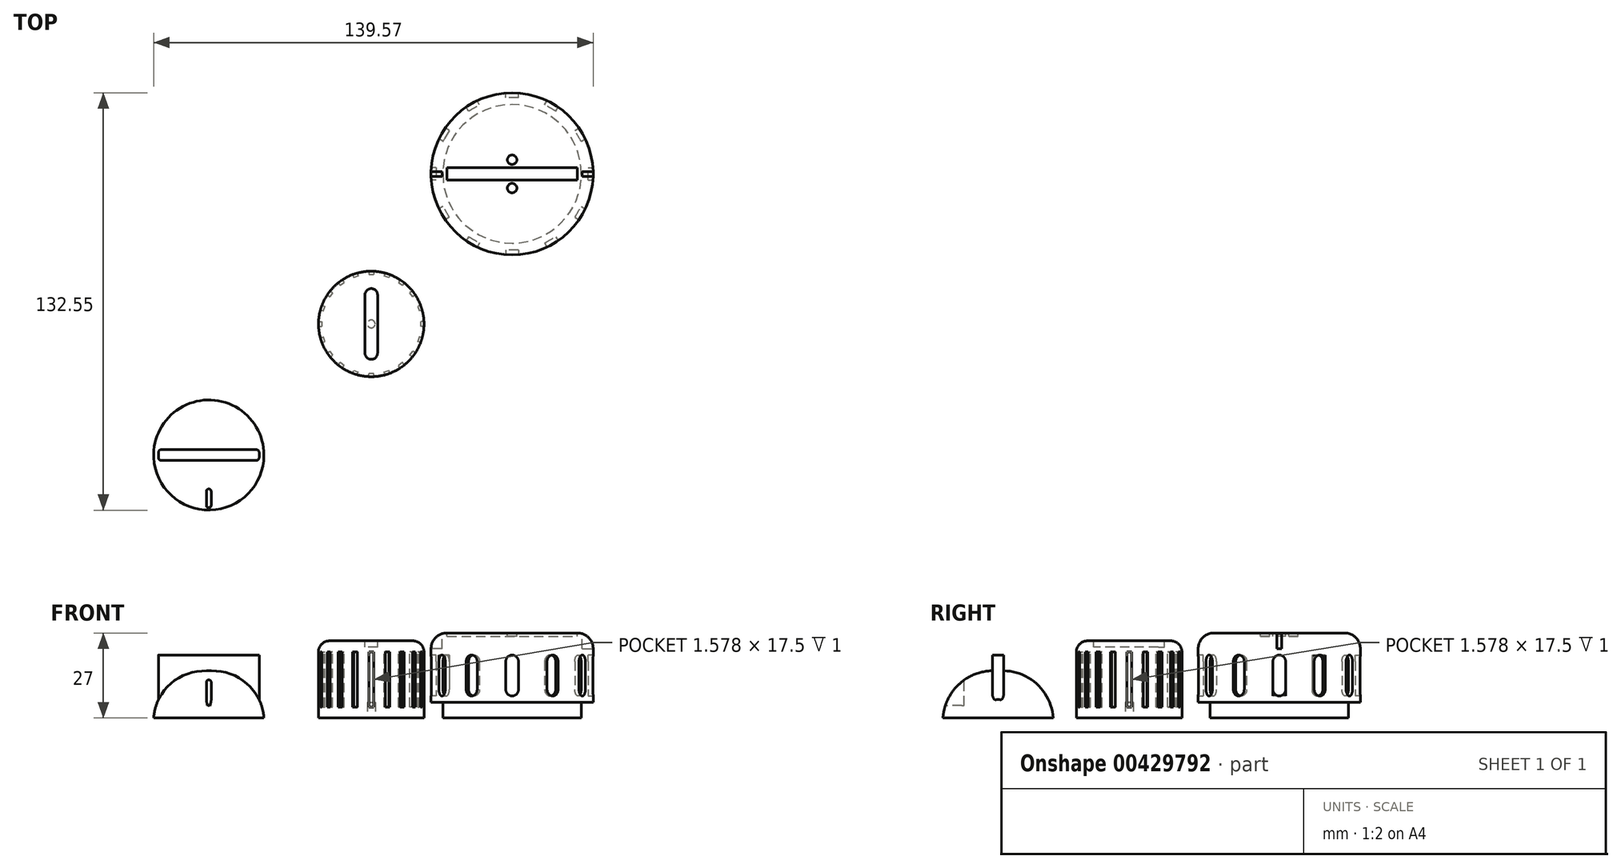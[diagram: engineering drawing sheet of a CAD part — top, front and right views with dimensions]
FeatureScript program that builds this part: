
annotation { "Feature Type Name" : "Feature", "Feature Type Description" : "" }
export const myFeature = defineFeature(function(context is Context, id is Id, definition is map)
    precondition{}
    {
        {
            var Q0;
            Q0=qCreatedBy(makeId("Top.planeOp"),FACE);
            var sketch = newSketch(context, id + "F0", { "sketchPlane" : qUnion([Q0])});
            skCircle(sketch, "E0", {"center": v(0, 0) * mm, "radius": 16.75 * mm});
            skSolve(sketch);
        }
        {
            var Q0;
            Q0=makeQuery(id+"F0.imprint","IMPRINT",FACE,{"disambiguationData":[TD([[makeQuery(id+"F0.imprint","IMPRINT",EDGE,{"derivedFrom":sQuery(id+"F0.wireOp",EDGE,"E0")}),1.0]])]});
            extrude(context, id + "F1", {"entities" : qUnion([Q0]), "depth" : 21 * mm});
        }
        {
            var Q0;
            Q0=makeQuery(id+"F1.opExtrude","CAP_FACE",FACE,{"disambiguationData":[OSD([sQuery(id+"F0.wireOp",EDGE,"E0")])],"isStart":false});
            var sketch = newSketch(context, id + "F2", { "sketchPlane" : qUnion([Q0])});
            skSolve(sketch);
        }
        {
            var Q0;
            Q0=makeQuery(id+"F1.opExtrude","CAP_FACE",FACE,{"disambiguationData":[OSD([sQuery(id+"F0.wireOp",EDGE,"E0")])],"isStart":false});
            var sketch = newSketch(context, id + "F3", { "sketchPlane" : qUnion([Q0])});
            skLineSegment(sketch, "E1", {"start": v(0, 0) * mm, "end": v(0, 16.75) * mm, "construction": true});
            skLineSegment(sketch, "E2", {"start": v(0, 0) * mm, "end": v(-0.79, 16.73) * mm, "construction": true});
            skLineSegment(sketch, "E3", {"start": v(0, 0) * mm, "end": v(0.79, 16.73) * mm, "construction": true});
            skLineSegment(sketch, "E4", {"start": v(0, 0) * mm, "end": v(4.42, 16.16) * mm, "construction": true});
            skLineSegment(sketch, "E5", {"start": v(0.79, 16.73) * mm, "end": v(0.79, 15.73) * mm});
            skLineSegment(sketch, "E6", {"start": v(-0.79, 16.73) * mm, "end": v(-0.79, 15.73) * mm});
            skLineSegment(sketch, "E7", {"start": v(-0.79, 15.73) * mm, "end": v(0.79, 15.73) * mm});
            skArc(sketch, "E8", {"start": v(0.79, 16.73) * mm, "mid": v(0, 16.75) * mm, "end": v(-0.79, 16.73) * mm});
            skLineSegment(sketch, "E9", {"start": v(0, 0) * mm, "end": v(2.62, 16.54) * mm, "construction": true});
            skArc(sketch, "E10.MirrorCS", {"start": v(4.42, 16.16) * mm, "mid": v(5.18, 15.93) * mm, "end": v(5.92, 15.67) * mm});
            skLineSegment(sketch, "E11.MirrorCS", {"start": v(4.42, 16.16) * mm, "end": v(4.11, 15.2) * mm});
            skLineSegment(sketch, "E12.MirrorCS", {"start": v(5.92, 15.67) * mm, "end": v(5.61, 14.72) * mm});
            skLineSegment(sketch, "E13.MirrorCS", {"start": v(5.61, 14.72) * mm, "end": v(4.11, 15.2) * mm});
            skLineSegment(sketch, "E14", {"start": v(0, 0) * mm, "end": v(7.6, 14.92) * mm, "construction": true});
            skLineSegment(sketch, "E15.MirrorCS", {"start": v(10.47, 13.07) * mm, "end": v(9.89, 12.26) * mm});
            skLineSegment(sketch, "E16.MirrorCS", {"start": v(8.6, 13.2) * mm, "end": v(9.89, 12.26) * mm});
            skLineSegment(sketch, "E17.MirrorCS", {"start": v(9.2, 14) * mm, "end": v(8.6, 13.2) * mm});
            skArc(sketch, "E18.MirrorCS", {"start": v(10.47, 13.07) * mm, "mid": v(9.85, 13.55) * mm, "end": v(9.2, 14) * mm});
            skArc(sketch, "E19.MirrorCS", {"start": v(13.07, 10.47) * mm, "mid": v(13.55, 9.85) * mm, "end": v(14, 9.2) * mm});
            skLineSegment(sketch, "E20.MirrorCS", {"start": v(13.07, 10.47) * mm, "end": v(12.26, 9.89) * mm});
            skLineSegment(sketch, "E21.MirrorCS", {"start": v(14, 9.2) * mm, "end": v(13.2, 8.6) * mm});
            skLineSegment(sketch, "E22.MirrorCS", {"start": v(13.2, 8.6) * mm, "end": v(12.26, 9.89) * mm});
            skLineSegment(sketch, "E23", {"start": v(13.07, 10.47) * mm, "end": v(0, 0) * mm, "construction": true});
            skLineSegment(sketch, "E24", {"start": v(14.92, 7.6) * mm, "end": v(0, 0) * mm, "construction": true});
            skArc(sketch, "E25.MirrorCS", {"start": v(16.16, 4.42) * mm, "mid": v(15.93, 5.18) * mm, "end": v(15.67, 5.92) * mm});
            skLineSegment(sketch, "E26.MirrorCS", {"start": v(15.67, 5.92) * mm, "end": v(14.72, 5.61) * mm});
            skLineSegment(sketch, "E27.MirrorCS", {"start": v(14.72, 5.61) * mm, "end": v(15.2, 4.11) * mm});
            skLineSegment(sketch, "E28.MirrorCS", {"start": v(16.16, 4.42) * mm, "end": v(15.2, 4.11) * mm});
            skLineSegment(sketch, "E29.MirrorCS", {"start": v(16.73, -0.79) * mm, "end": v(15.73, -0.79) * mm});
            skLineSegment(sketch, "E30.MirrorCS", {"start": v(15.73, -0.79) * mm, "end": v(15.73, 0.79) * mm});
            skLineSegment(sketch, "E31.MirrorCS", {"start": v(16.73, 0.79) * mm, "end": v(15.73, 0.79) * mm});
            skArc(sketch, "E32.MirrorCS", {"start": v(16.73, 0.79) * mm, "mid": v(16.75, 0) * mm, "end": v(16.73, -0.79) * mm});
            skArc(sketch, "E33.MirrorCS", {"start": v(15.67, -5.92) * mm, "mid": v(15.93, -5.18) * mm, "end": v(16.16, -4.42) * mm});
            skLineSegment(sketch, "E34.MirrorCS", {"start": v(16.16, -4.42) * mm, "end": v(15.2, -4.11) * mm});
            skLineSegment(sketch, "E35.MirrorCS", {"start": v(15.2, -4.11) * mm, "end": v(14.72, -5.61) * mm});
            skLineSegment(sketch, "E36.MirrorCS", {"start": v(15.67, -5.92) * mm, "end": v(14.72, -5.61) * mm});
            skArc(sketch, "E37.MirrorCS", {"start": v(14, -9.2) * mm, "mid": v(13.55, -9.85) * mm, "end": v(13.07, -10.47) * mm});
            skLineSegment(sketch, "E38.MirrorCS", {"start": v(13.07, -10.47) * mm, "end": v(12.26, -9.89) * mm});
            skLineSegment(sketch, "E39.MirrorCS", {"start": v(14, -9.2) * mm, "end": v(13.2, -8.6) * mm});
            skLineSegment(sketch, "E40.MirrorCS", {"start": v(12.26, -9.89) * mm, "end": v(13.2, -8.6) * mm});
            skLineSegment(sketch, "E41", {"start": v(0, 0) * mm, "end": v(14, -9.2) * mm, "construction": true});
            skLineSegment(sketch, "E42", {"start": v(0, 0) * mm, "end": v(11.84, -11.84) * mm, "construction": true});
            skLineSegment(sketch, "E43.MirrorCS", {"start": v(-10.47, -13.07) * mm, "end": v(-9.89, -12.26) * mm});
            skLineSegment(sketch, "E44.MirrorCS", {"start": v(-0.79, -16.73) * mm, "end": v(-0.79, -15.73) * mm});
            skArc(sketch, "E45.MirrorCS", {"start": v(-10.47, -13.07) * mm, "mid": v(-9.85, -13.55) * mm, "end": v(-9.2, -14) * mm});
            skLineSegment(sketch, "E46.MirrorCS", {"start": v(-13.07, -10.47) * mm, "end": v(-12.26, -9.89) * mm});
            skLineSegment(sketch, "E47.MirrorCS", {"start": v(-13.2, -8.6) * mm, "end": v(-12.26, -9.89) * mm});
            skLineSegment(sketch, "E48.MirrorCS", {"start": v(-16.16, -4.42) * mm, "end": v(-15.2, -4.11) * mm});
            skLineSegment(sketch, "E49.MirrorCS", {"start": v(-5.61, -14.72) * mm, "end": v(-4.11, -15.2) * mm});
            skLineSegment(sketch, "E50.MirrorCS", {"start": v(9.89, -12.26) * mm, "end": v(8.6, -13.2) * mm});
            skLineSegment(sketch, "E51.MirrorCS", {"start": v(-5.92, -15.67) * mm, "end": v(-5.61, -14.72) * mm});
            skLineSegment(sketch, "E52.MirrorCS", {"start": v(-16.73, 0.79) * mm, "end": v(-15.73, 0.79) * mm});
            skLineSegment(sketch, "E53.MirrorCS", {"start": v(0.79, -15.73) * mm, "end": v(-0.79, -15.73) * mm});
            skLineSegment(sketch, "E54.MirrorCS", {"start": v(4.11, -15.2) * mm, "end": v(5.61, -14.72) * mm});
            skArc(sketch, "E55.MirrorCS", {"start": v(-4.42, -16.16) * mm, "mid": v(-5.18, -15.93) * mm, "end": v(-5.92, -15.67) * mm});
            skLineSegment(sketch, "E56.MirrorCS", {"start": v(-9.2, -14) * mm, "end": v(-8.6, -13.2) * mm});
            skLineSegment(sketch, "E57.MirrorCS", {"start": v(-8.6, -13.2) * mm, "end": v(-9.89, -12.26) * mm});
            skLineSegment(sketch, "E58.MirrorCS", {"start": v(5.92, -15.67) * mm, "end": v(5.61, -14.72) * mm});
            skLineSegment(sketch, "E59.MirrorCS", {"start": v(-15.67, -5.92) * mm, "end": v(-14.72, -5.61) * mm});
            skArc(sketch, "E60.MirrorCS", {"start": v(5.92, -15.67) * mm, "mid": v(5.18, -15.93) * mm, "end": v(4.42, -16.16) * mm});
            skLineSegment(sketch, "E61.MirrorCS", {"start": v(-14, -9.2) * mm, "end": v(-13.2, -8.6) * mm});
            skLineSegment(sketch, "E62.MirrorCS", {"start": v(-4.42, -16.16) * mm, "end": v(-4.11, -15.2) * mm});
            skLineSegment(sketch, "E63.MirrorCS", {"start": v(-16.73, -0.79) * mm, "end": v(-15.73, -0.79) * mm});
            skArc(sketch, "E64.MirrorCS", {"start": v(9.2, -14) * mm, "mid": v(9.85, -13.55) * mm, "end": v(10.47, -13.07) * mm});
            skLineSegment(sketch, "E65.MirrorCS", {"start": v(0.79, -16.73) * mm, "end": v(0.79, -15.73) * mm});
            skArc(sketch, "E66.MirrorCS", {"start": v(-0.79, -16.73) * mm, "mid": v(0, -16.75) * mm, "end": v(0.79, -16.73) * mm});
            skLineSegment(sketch, "E67.MirrorCS", {"start": v(4.42, -16.16) * mm, "end": v(4.11, -15.2) * mm});
            skLineSegment(sketch, "E68.MirrorCS", {"start": v(9.2, -14) * mm, "end": v(8.6, -13.2) * mm});
            skLineSegment(sketch, "E69.MirrorCS", {"start": v(-15.73, 0.79) * mm, "end": v(-15.73, -0.79) * mm});
            skLineSegment(sketch, "E70.MirrorCS", {"start": v(10.47, -13.07) * mm, "end": v(9.89, -12.26) * mm});
            skArc(sketch, "E71.MirrorCS", {"start": v(-16.73, -0.79) * mm, "mid": v(-16.75, 0) * mm, "end": v(-16.73, 0.79) * mm});
            skLineSegment(sketch, "E72.MirrorCS", {"start": v(-14.72, -5.61) * mm, "end": v(-15.2, -4.11) * mm});
            skArc(sketch, "E73.MirrorCS", {"start": v(-13.07, -10.47) * mm, "mid": v(-13.55, -9.85) * mm, "end": v(-14, -9.2) * mm});
            skArc(sketch, "E74.MirrorCS", {"start": v(-16.16, -4.42) * mm, "mid": v(-15.93, -5.18) * mm, "end": v(-15.67, -5.92) * mm});
            skLineSegment(sketch, "E75.MirrorCS", {"start": v(0, 0) * mm, "end": v(-16.73, -0.79) * mm, "construction": true});
            skLineSegment(sketch, "E76", {"start": v(0, 0) * mm, "end": v(-16.54, 2.62) * mm, "construction": true});
            skLineSegment(sketch, "E77.MirrorCS", {"start": v(-13.07, 10.47) * mm, "end": v(-12.26, 9.89) * mm});
            skLineSegment(sketch, "E78.MirrorCS", {"start": v(-16.16, 4.42) * mm, "end": v(-15.2, 4.11) * mm});
            skLineSegment(sketch, "E79.MirrorCS", {"start": v(-9.2, 14) * mm, "end": v(-8.6, 13.2) * mm});
            skLineSegment(sketch, "E80.MirrorCS", {"start": v(-4.42, 16.16) * mm, "end": v(-4.11, 15.2) * mm});
            skLineSegment(sketch, "E81.MirrorCS", {"start": v(-10.47, 13.07) * mm, "end": v(-9.89, 12.26) * mm});
            skLineSegment(sketch, "E82.MirrorCS", {"start": v(-14, 9.2) * mm, "end": v(-13.2, 8.6) * mm});
            skLineSegment(sketch, "E83.MirrorCS", {"start": v(-5.92, 15.67) * mm, "end": v(-5.61, 14.72) * mm});
            skLineSegment(sketch, "E84.MirrorCS", {"start": v(-15.67, 5.92) * mm, "end": v(-14.72, 5.61) * mm});
            skArc(sketch, "E85.MirrorCS", {"start": v(-14, 9.2) * mm, "mid": v(-13.55, 9.85) * mm, "end": v(-13.07, 10.47) * mm});
            skLineSegment(sketch, "E86.MirrorCS", {"start": v(-4.11, 15.2) * mm, "end": v(-5.61, 14.72) * mm});
            skLineSegment(sketch, "E87.MirrorCS", {"start": v(-12.26, 9.89) * mm, "end": v(-13.2, 8.6) * mm});
            skArc(sketch, "E88.MirrorCS", {"start": v(-9.2, 14) * mm, "mid": v(-9.85, 13.55) * mm, "end": v(-10.47, 13.07) * mm});
            skLineSegment(sketch, "E89.MirrorCS", {"start": v(-9.89, 12.26) * mm, "end": v(-8.6, 13.2) * mm});
            skLineSegment(sketch, "E90.MirrorCS", {"start": v(-15.2, 4.11) * mm, "end": v(-14.72, 5.61) * mm});
            skArc(sketch, "E91.MirrorCS", {"start": v(-15.67, 5.92) * mm, "mid": v(-15.93, 5.18) * mm, "end": v(-16.16, 4.42) * mm});
            skArc(sketch, "E92.MirrorCS", {"start": v(-5.92, 15.67) * mm, "mid": v(-5.18, 15.93) * mm, "end": v(-4.42, 16.16) * mm});
            skLineSegment(sketch, "E93", {"start": v(-5.92, 15.67) * mm, "end": v(0, 0) * mm, "construction": true});
            skSolve(sketch);
        }
        {
            var Q0;
            Q0=qSketchRegion(id+"F3",true);
            extrude(context, id + "F4", {"entities" : qUnion([Q0]), "operationType" : NewBodyOperationType.REMOVE, "oppositeDirection" : true, "depth" : 17.5 * mm});
        }
        {
            var Q0;
            Q0=makeQuery(id+"F2.imprint","IMPRINT",FACE,{"disambiguationData":[TD([[makeQuery(id+"F2.imprint","IMPRINT",EDGE,{"derivedFrom":makeQuery(id+"F1.opExtrude","CAP_EDGE",EDGE,{"disambiguationData":[OSD([sQuery(id+"F0.wireOp",EDGE,"E0")])],"isStart":false})}),1.0]])]});
            extrude(context, id + "F5", {"entities" : qUnion([Q0]), "operationType" : NewBodyOperationType.ADD, "depth" : 3.5 * mm});
        }
        {
            var Q0;
            Q0=makeQuery(id+"F5.opExtrude","CAP_FACE",FACE,{"disambiguationData":[OSD([sQuery(id+"F0.wireOp",EDGE,"E0")])],"isStart":false});
            var sketch = newSketch(context, id + "F6", { "sketchPlane" : qUnion([Q0])});
            skLineSegment(sketch, "E94", {"start": v(-2, 0) * mm, "end": v(2, 0) * mm, "construction": true});
            skLineSegment(sketch, "E95", {"start": v(-2, 9.25) * mm, "end": v(-2, -9.25) * mm});
            skLineSegment(sketch, "E96", {"start": v(2, 9.25) * mm, "end": v(2, -9.25) * mm});
            skArc(sketch, "E97", {"start": v(2, 9.25) * mm, "mid": v(0, 11.25) * mm, "end": v(-2, 9.25) * mm});
            skArc(sketch, "E98", {"start": v(-2, -9.25) * mm, "mid": v(0, -11.25) * mm, "end": v(2, -9.25) * mm});
            skLineSegment(sketch, "E99", {"start": v(0, -11.25) * mm, "end": v(0, 11.25) * mm, "construction": true});
            skSolve(sketch);
        }
        {
            var Q0;
            Q0=qSketchRegion(id+"F6",true);
            extrude(context, id + "F7", {"entities" : qUnion([Q0]), "operationType" : NewBodyOperationType.REMOVE, "oppositeDirection" : true, "depth" : 2 * mm});
        }
        {
            var Q0;
            Q0=makeQuery(id+"F1.opExtrude","CAP_FACE",FACE,{"disambiguationData":[OSD([sQuery(id+"F0.wireOp",EDGE,"E0")])],"isStart":true});
            var sketch = newSketch(context, id + "F8", { "sketchPlane" : qUnion([Q0])});
            skCircle(sketch, "E100", {"center": v(0, 0) * mm, "radius": 1.25 * mm});
            skSolve(sketch);
        }
        {
            var Q0;
            Q0=qSketchRegion(id+"F8",true);
            extrude(context, id + "F9", {"entities" : qUnion([Q0]), "operationType" : NewBodyOperationType.REMOVE, "oppositeDirection" : true, "depth" : 5 * mm});
        }
        {
            var Q0;
            Q0=makeQuery(id+"F5.opExtrude","CAP_EDGE",EDGE,{"disambiguationData":[OSD([sQuery(id+"F0.wireOp",EDGE,"E0")])],"isStart":false});
            fillet(context, id + "F10", {"entities" : qUnion([Q0]), "radius" : 3.5 * mm, "tangentPropagation" : true, "allowEdgeOverflow" : false});
        }
        {
            var Q0;
            Q0=qCreatedBy(makeId("Top.planeOp"),FACE);
            var sketch = newSketch(context, id + "F11", { "sketchPlane" : qUnion([Q0])});
            skCircle(sketch, "E101", {"center": v(-51.59, -41.64) * mm, "radius": 17.5 * mm});
            skSolve(sketch);
        }
        {
            var Q0;
            Q0=makeQuery(id+"F11.imprint","IMPRINT",FACE,{"disambiguationData":[TD([[makeQuery(id+"F11.imprint","IMPRINT",EDGE,{"derivedFrom":sQuery(id+"F11.wireOp",EDGE,"E101")}),1.0]])]});
            extrude(context, id + "F12", {"entities" : qUnion([Q0]), "depth" : 15 * mm});
        }
        {
            var Q0;
            Q0=makeQuery(id+"F12.opExtrude","CAP_FACE",FACE,{"disambiguationData":[OSD([sQuery(id+"F11.wireOp",EDGE,"E101")])],"isStart":false});
            fillet(context, id + "F13", {"entities" : qUnion([Q0]), "radius" : 16 * mm, "tangentPropagation" : true, "allowEdgeOverflow" : false});
        }
        {
            var Q0;
            Q0=makeQuery(id+"F12.opExtrude","CAP_FACE",FACE,{"disambiguationData":[OSD([sQuery(id+"F11.wireOp",EDGE,"E101")])],"isStart":false});
            var sketch = newSketch(context, id + "F14", { "sketchPlane" : qUnion([Q0])});
            skLineSegment(sketch, "E102.bottom", {"start": v(-35.59, -43.39) * mm, "end": v(-67.59, -43.39) * mm});
            skLineSegment(sketch, "E102.top", {"start": v(-35.59, -39.89) * mm, "end": v(-67.59, -39.89) * mm});
            skLineSegment(sketch, "E102.left", {"start": v(-35.59, -43.39) * mm, "end": v(-35.59, -39.89) * mm});
            skLineSegment(sketch, "E102.right", {"start": v(-67.59, -43.39) * mm, "end": v(-67.59, -39.89) * mm});
            skPoint(sketch, "E102.middle", {"position": v(-51.59, -41.64) * mm});
            skSolve(sketch);
        }
        {
            var Q0;
            Q0=qSketchRegion(id+"F14",true);
            var Q1;
            Q1=makeQuery(id+"F12.opExtrude","CAP_FACE",FACE,{"disambiguationData":[OSD([sQuery(id+"F11.wireOp",EDGE,"E101")])],"isStart":true});
            extrude(context, id + "F15", {"entities" : qUnion([Q0]), "operationType" : NewBodyOperationType.ADD, "depth" : 5 * mm, "hasSecondDirection" : true, "secondDirectionBound" : SecondDirectionBoundingType.UP_TO_SURFACE, "secondDirectionOppositeDirection" : true, "secondDirectionBoundEntityFace" : qUnion([Q1]), "secondDirectionDepth" : 25 * mm});
        }
        {
            var Q0;
            Q0=makeQuery(id+"F15.opExtrude","SWEPT_EDGE",EDGE,{"disambiguationData":[OSD([sQuery(id+"F14.wireOp",EDGE,"E102.bottom"),sQuery(id+"F14.wireOp",EDGE,"E102.right")])]});
            var Q1;
            Q1=makeQuery(id+"F15.opExtrude","SWEPT_EDGE",EDGE,{"disambiguationData":[OSD([sQuery(id+"F14.wireOp",EDGE,"E102.bottom"),sQuery(id+"F14.wireOp",EDGE,"E102.left")])]});
            var Q2;
            Q2=makeQuery(id+"F15.opExtrude","SWEPT_EDGE",EDGE,{"disambiguationData":[OSD([sQuery(id+"F14.wireOp",EDGE,"E102.top"),sQuery(id+"F14.wireOp",EDGE,"E102.left")])]});
            var Q3;
            Q3=makeQuery(id+"F15.opExtrude","SWEPT_EDGE",EDGE,{"disambiguationData":[OSD([sQuery(id+"F14.wireOp",EDGE,"E102.top"),sQuery(id+"F14.wireOp",EDGE,"E102.right")])]});
            fillet(context, id + "F16", {"entities" : qUnion([Q0, Q1, Q2, Q3]), "radius" : 1 * mm, "tangentPropagation" : true, "allowEdgeOverflow" : false});
        }
        {
            var Q0;
            Q0=makeQuery(id+"F15.opExtrude","CAP_FACE",FACE,{"disambiguationData":[OSD([sQuery(id+"F14.wireOp",EDGE,"E102.bottom"),sQuery(id+"F14.wireOp",EDGE,"E102.top"),sQuery(id+"F14.wireOp",EDGE,"E102.left"),sQuery(id+"F14.wireOp",EDGE,"E102.right")])],"isStart":false});
            var sketch = newSketch(context, id + "F17", { "sketchPlane" : qUnion([Q0])});
            skLineSegment(sketch, "E103", {"start": v(-51.59, -43.39) * mm, "end": v(-51.59, -52.39) * mm, "construction": true});
            skLineSegment(sketch, "E104", {"start": v(-51.59, -52.39) * mm, "end": v(-51.59, -52.39) * mm});
            skLineSegment(sketch, "E105", {"start": v(-51.59, -52.39) * mm, "end": v(-51.59, -58.39) * mm, "construction": true});
            skLineSegment(sketch, "E106", {"start": v(-52.34, -55.39) * mm, "end": v(-50.59, -55.39) * mm, "construction": true});
            skLineSegment(sketch, "E107.MirrorCS", {"start": v(-51.59, -58.39) * mm, "end": v(-51.59, -58.39) * mm});
            skLineSegment(sketch, "E108", {"start": v(-52.34, -53.14) * mm, "end": v(-52.34, -57.64) * mm});
            skArc(sketch, "E109", {"start": v(-51.59, -58.39) * mm, "mid": v(-52.12, -58.17) * mm, "end": v(-52.34, -57.64) * mm});
            skLineSegment(sketch, "E110.MirrorCS", {"start": v(-50.84, -53.14) * mm, "end": v(-50.84, -57.64) * mm});
            skArc(sketch, "E111.MirrorCS", {"start": v(-51.59, -58.39) * mm, "mid": v(-51.06, -58.17) * mm, "end": v(-50.84, -57.64) * mm});
            skArc(sketch, "E112.MirrorCS", {"start": v(-51.59, -52.39) * mm, "mid": v(-52.12, -52.6) * mm, "end": v(-52.34, -53.14) * mm});
            skArc(sketch, "E113.MirrorCS", {"start": v(-51.59, -52.39) * mm, "mid": v(-51.06, -52.6) * mm, "end": v(-50.84, -53.14) * mm});
            skSolve(sketch);
        }
        {
            var Q0;
            Q0=qSketchRegion(id+"F17",true);
            extrude(context, id + "F18", {"entities" : qUnion([Q0]), "operationType" : NewBodyOperationType.REMOVE, "oppositeDirection" : true, "depth" : 16 * mm});
        }
        {
            var Q0;
            Q0=qCreatedBy(makeId("Top.planeOp"),FACE);
            var sketch = newSketch(context, id + "F19", { "sketchPlane" : qUnion([Q0])});
            skCircle(sketch, "E114", {"center": v(44.73, 47.66) * mm, "radius": 22 * mm});
            skSolve(sketch);
        }
        {
            var Q0;
            Q0=makeQuery(id+"F19.imprint","IMPRINT",FACE,{"disambiguationData":[TD([[makeQuery(id+"F19.imprint","IMPRINT",EDGE,{"derivedFrom":sQuery(id+"F19.wireOp",EDGE,"E114")}),1.0]])]});
            extrude(context, id + "F20", {"entities" : qUnion([Q0]), "depth" : 5 * mm});
        }
        {
            var Q0;
            Q0=makeQuery(id+"F20.opExtrude","CAP_FACE",FACE,{"disambiguationData":[OSD([sQuery(id+"F19.wireOp",EDGE,"E114")])],"isStart":false});
            var sketch = newSketch(context, id + "F21", { "sketchPlane" : qUnion([Q0])});
            skCircle(sketch, "E115", {"center": v(44.73, 47.66) * mm, "radius": 25.75 * mm});
            skSolve(sketch);
        }
        {
            var Q0;
            Q0=makeQuery(id+"F21.imprint","IMPRINT",FACE,{"disambiguationData":[TD([[makeQuery(id+"F21.imprint","IMPRINT",EDGE,{"derivedFrom":sQuery(id+"F21.wireOp",EDGE,"E115")}),1.0]])]});
            var Q1;
            Q1=makeQuery(id+"F21.imprint","IMPRINT",FACE,{"disambiguationData":[TD([[makeQuery(id+"F21.imprint","IMPRINT",EDGE,{"derivedFrom":makeQuery(id+"F20.opExtrude","CAP_EDGE",EDGE,{"disambiguationData":[OSD([sQuery(id+"F19.wireOp",EDGE,"E114")])],"isStart":false})}),1.0]])]});
            extrude(context, id + "F22", {"entities" : qUnion([Q0, Q1]), "operationType" : NewBodyOperationType.ADD, "depth" : 2 * mm});
        }
        {
            var Q0;
            Q0=makeQuery(id+"F22.opExtrude","CAP_FACE",FACE,{"disambiguationData":[OSD([sQuery(id+"F21.wireOp",EDGE,"E115")])],"isStart":false});
            var sketch = newSketch(context, id + "F23", { "sketchPlane" : qUnion([Q0])});
            skPoint(sketch, "E116", {"position": v(44.73, 47.66) * mm});
            skLineSegment(sketch, "E117", {"start": v(18.98, 47.66) * mm, "end": v(70.48, 47.66) * mm, "construction": true});
            skLineSegment(sketch, "E118", {"start": v(44.73, 73.4) * mm, "end": v(44.73, 21.9) * mm, "construction": true});
            skLineSegment(sketch, "E119", {"start": v(20.56, 49.66) * mm, "end": v(20.56, 45.66) * mm});
            skPoint(sketch, "E120", {"position": v(20.56, 47.66) * mm});
            skLineSegment(sketch, "E121", {"start": v(20.56, 45.66) * mm, "end": v(19.06, 45.66) * mm});
            skLineSegment(sketch, "E122", {"start": v(20.56, 49.66) * mm, "end": v(19.06, 49.66) * mm});
            skLineSegment(sketch, "E123", {"start": v(44.73, 47.66) * mm, "end": v(31.85, 25.36) * mm, "construction": true});
            skLineSegment(sketch, "E124", {"start": v(22.43, 34.78) * mm, "end": v(44.73, 47.66) * mm, "construction": true});
            skLineSegment(sketch, "E125", {"start": v(19.85, 41) * mm, "end": v(44.73, 47.66) * mm, "construction": true});
            skLineSegment(sketch, "E126.MirrorCS", {"start": v(24.8, 33.84) * mm, "end": v(23.5, 33.09) * mm});
            skLineSegment(sketch, "E127.MirrorCS", {"start": v(22.8, 37.3) * mm, "end": v(21.5, 36.55) * mm});
            skLineSegment(sketch, "E128.MirrorCS", {"start": v(24.8, 33.84) * mm, "end": v(22.8, 37.3) * mm});
            skLineSegment(sketch, "E129", {"start": v(26.52, 29.45) * mm, "end": v(44.73, 47.66) * mm, "construction": true});
            skLineSegment(sketch, "E130.MirrorCS", {"start": v(34.37, 25.72) * mm, "end": v(33.62, 24.42) * mm});
            skLineSegment(sketch, "E131.MirrorCS", {"start": v(30.9, 27.72) * mm, "end": v(30.16, 26.42) * mm});
            skLineSegment(sketch, "E132.MirrorCS", {"start": v(30.9, 27.72) * mm, "end": v(34.37, 25.72) * mm});
            skLineSegment(sketch, "E133", {"start": v(38.06, 22.78) * mm, "end": v(44.73, 47.66) * mm, "construction": true});
            skLineSegment(sketch, "E134.MirrorCS", {"start": v(46.73, 23.48) * mm, "end": v(46.73, 21.98) * mm});
            skLineSegment(sketch, "E135.MirrorCS", {"start": v(46.73, 23.48) * mm, "end": v(42.73, 23.48) * mm});
            skLineSegment(sketch, "E136.MirrorCS", {"start": v(42.73, 23.48) * mm, "end": v(42.73, 21.98) * mm});
            skLineSegment(sketch, "E137.MirrorCS", {"start": v(46.73, 71.83) * mm, "end": v(46.73, 73.33) * mm});
            skLineSegment(sketch, "E138.MirrorCS", {"start": v(46.73, 71.83) * mm, "end": v(42.73, 71.83) * mm});
            skLineSegment(sketch, "E139.MirrorCS", {"start": v(42.73, 71.83) * mm, "end": v(42.73, 73.33) * mm});
            skLineSegment(sketch, "E140.MirrorCS", {"start": v(34.37, 69.6) * mm, "end": v(33.62, 70.89) * mm});
            skLineSegment(sketch, "E141.MirrorCS", {"start": v(30.9, 67.6) * mm, "end": v(34.37, 69.6) * mm});
            skLineSegment(sketch, "E142.MirrorCS", {"start": v(30.9, 67.6) * mm, "end": v(30.16, 68.89) * mm});
            skLineSegment(sketch, "E143.MirrorCS", {"start": v(24.8, 61.47) * mm, "end": v(23.5, 62.22) * mm});
            skLineSegment(sketch, "E144.MirrorCS", {"start": v(24.8, 61.47) * mm, "end": v(22.8, 58.01) * mm});
            skLineSegment(sketch, "E145.MirrorCS", {"start": v(22.8, 58.01) * mm, "end": v(21.5, 58.76) * mm});
            skLineSegment(sketch, "E146.MirrorCS", {"start": v(55.08, 69.6) * mm, "end": v(55.83, 70.89) * mm});
            skLineSegment(sketch, "E147.MirrorCS", {"start": v(58.55, 67.6) * mm, "end": v(55.08, 69.6) * mm});
            skLineSegment(sketch, "E148.MirrorCS", {"start": v(58.55, 67.6) * mm, "end": v(59.3, 68.89) * mm});
            skLineSegment(sketch, "E149.MirrorCS", {"start": v(64.66, 61.47) * mm, "end": v(65.96, 62.22) * mm});
            skLineSegment(sketch, "E150.MirrorCS", {"start": v(66.66, 58.01) * mm, "end": v(67.96, 58.76) * mm});
            skLineSegment(sketch, "E151.MirrorCS", {"start": v(64.66, 61.47) * mm, "end": v(66.66, 58.01) * mm});
            skLineSegment(sketch, "E152.MirrorCS", {"start": v(68.9, 49.66) * mm, "end": v(70.4, 49.66) * mm});
            skLineSegment(sketch, "E153.MirrorCS", {"start": v(68.9, 49.66) * mm, "end": v(68.9, 45.66) * mm});
            skLineSegment(sketch, "E154.MirrorCS", {"start": v(68.9, 45.66) * mm, "end": v(70.4, 45.66) * mm});
            skLineSegment(sketch, "E155.MirrorCS", {"start": v(66.66, 37.3) * mm, "end": v(67.96, 36.55) * mm});
            skLineSegment(sketch, "E156.MirrorCS", {"start": v(64.66, 33.84) * mm, "end": v(66.66, 37.3) * mm});
            skLineSegment(sketch, "E157.MirrorCS", {"start": v(64.66, 33.84) * mm, "end": v(65.96, 33.09) * mm});
            skLineSegment(sketch, "E158.MirrorCS", {"start": v(58.55, 27.72) * mm, "end": v(59.3, 26.42) * mm});
            skLineSegment(sketch, "E159.MirrorCS", {"start": v(55.08, 25.72) * mm, "end": v(55.83, 24.42) * mm});
            skLineSegment(sketch, "E160.MirrorCS", {"start": v(58.55, 27.72) * mm, "end": v(55.08, 25.72) * mm});
            skSolve(sketch);
        }
        {
            var Q0;
            Q0=makeQuery(id+"F23.imprint","IMPRINT",FACE,{"disambiguationData":[TD([[makeQuery(id+"F23.imprint","IMPRINT",EDGE,{"derivedFrom":sQuery(id+"F23.wireOp",EDGE,"E119")}),1.0]])]});
            extrude(context, id + "F24", {"entities" : qUnion([Q0]), "operationType" : NewBodyOperationType.ADD, "depth" : 13 * mm});
        }
        {
            var Q0;
            Q0=makeQuery(id+"F24.opExtrude","CAP_FACE",FACE,{"disambiguationData":[OSD([sQuery(id+"F21.wireOp",EDGE,"E115"),sQuery(id+"F23.wireOp",EDGE,"E119"),sQuery(id+"F23.wireOp",EDGE,"E121"),sQuery(id+"F23.wireOp",EDGE,"E122"),sQuery(id+"F23.wireOp",EDGE,"E126.MirrorCS"),sQuery(id+"F23.wireOp",EDGE,"E127.MirrorCS"),sQuery(id+"F23.wireOp",EDGE,"E128.MirrorCS"),sQuery(id+"F23.wireOp",EDGE,"E130.MirrorCS"),sQuery(id+"F23.wireOp",EDGE,"E131.MirrorCS"),sQuery(id+"F23.wireOp",EDGE,"E132.MirrorCS"),sQuery(id+"F23.wireOp",EDGE,"E134.MirrorCS"),sQuery(id+"F23.wireOp",EDGE,"E135.MirrorCS"),sQuery(id+"F23.wireOp",EDGE,"E136.MirrorCS"),sQuery(id+"F23.wireOp",EDGE,"E137.MirrorCS"),sQuery(id+"F23.wireOp",EDGE,"E138.MirrorCS"),sQuery(id+"F23.wireOp",EDGE,"E139.MirrorCS"),sQuery(id+"F23.wireOp",EDGE,"E140.MirrorCS"),sQuery(id+"F23.wireOp",EDGE,"E141.MirrorCS"),sQuery(id+"F23.wireOp",EDGE,"E142.MirrorCS"),sQuery(id+"F23.wireOp",EDGE,"E143.MirrorCS"),sQuery(id+"F23.wireOp",EDGE,"E144.MirrorCS"),sQuery(id+"F23.wireOp",EDGE,"E145.MirrorCS"),sQuery(id+"F23.wireOp",EDGE,"E146.MirrorCS"),sQuery(id+"F23.wireOp",EDGE,"E147.MirrorCS"),sQuery(id+"F23.wireOp",EDGE,"E148.MirrorCS"),sQuery(id+"F23.wireOp",EDGE,"E149.MirrorCS"),sQuery(id+"F23.wireOp",EDGE,"E150.MirrorCS"),sQuery(id+"F23.wireOp",EDGE,"E151.MirrorCS"),sQuery(id+"F23.wireOp",EDGE,"E152.MirrorCS"),sQuery(id+"F23.wireOp",EDGE,"E153.MirrorCS"),sQuery(id+"F23.wireOp",EDGE,"E154.MirrorCS"),sQuery(id+"F23.wireOp",EDGE,"E155.MirrorCS"),sQuery(id+"F23.wireOp",EDGE,"E156.MirrorCS"),sQuery(id+"F23.wireOp",EDGE,"E157.MirrorCS"),sQuery(id+"F23.wireOp",EDGE,"E158.MirrorCS"),sQuery(id+"F23.wireOp",EDGE,"E159.MirrorCS"),sQuery(id+"F23.wireOp",EDGE,"E160.MirrorCS")])],"isStart":false});
            var sketch = newSketch(context, id + "F25", { "sketchPlane" : qUnion([Q0])});
            skCircle(sketch, "E161", {"center": v(44.73, 47.66) * mm, "radius": 25.75 * mm});
            skSolve(sketch);
        }
        {
            var Q0;
            Q0=qSketchRegion(id+"F25",true);
            extrude(context, id + "F26", {"entities" : qUnion([Q0]), "operationType" : NewBodyOperationType.ADD, "depth" : 2 * mm});
        }
        {
            var Q0;
            Q0=makeQuery(id+"F26.opExtrude","CAP_FACE",FACE,{"disambiguationData":[OSD([sQuery(id+"F25.wireOp",EDGE,"E161")])],"isStart":false});
            extrude(context, id + "F27", {"entities" : qUnion([Q0]), "operationType" : NewBodyOperationType.ADD, "depth" : 5 * mm});
        }
        {
            var Q0;
            Q0=makeQuery(id+"F27.opExtrude","CAP_EDGE",EDGE,{"disambiguationData":[OSD([sQuery(id+"F25.wireOp",EDGE,"E161")])],"isStart":false});
            fillet(context, id + "F28", {"entities" : qUnion([Q0]), "radius" : 5 * mm, "tangentPropagation" : true, "allowEdgeOverflow" : false});
        }
        {
            var Q0;
            Q0=makeQuery(id+"F27.opExtrude","CAP_FACE",FACE,{"disambiguationData":[OSD([sQuery(id+"F25.wireOp",EDGE,"E161")])],"isStart":false});
            var sketch = newSketch(context, id + "F29", { "sketchPlane" : qUnion([Q0])});
            skPoint(sketch, "E162", {"position": v(44.73, 47.66) * mm});
            skLineSegment(sketch, "E163", {"start": v(44.73, 49.66) * mm, "end": v(44.73, 45.66) * mm, "construction": true});
            skLineSegment(sketch, "E164", {"start": v(24.07, 45.66) * mm, "end": v(65.38, 45.66) * mm});
            skLineSegment(sketch, "E165", {"start": v(24.07, 49.66) * mm, "end": v(65.38, 49.66) * mm});
            skCircle(sketch, "E166", {"center": v(44.73, 52.16) * mm, "radius": 1.5 * mm});
            skLineSegment(sketch, "E167", {"start": v(37.63, 47.66) * mm, "end": v(51.82, 47.66) * mm, "construction": true});
            skCircle(sketch, "E168.MirrorC", {"center": v(44.73, 43.16) * mm, "radius": 1.5 * mm});
            skSolve(sketch);
        }
        {
            var Q0;
            Q0=qSketchRegion(id+"F29",true);
            var Q1;
            {var subQ0=sQuery(id+"F29.wireOp",EDGE,"E164");Q1=makeQuery(id+"F29.imprint","IMPRINT",FACE,{"disambiguationData":[TD([[makeQuery(id+"F29.imprint","IMPRINT",EDGE,{"derivedFrom":subQ0}),1.0]])]});}
            extrude(context, id + "F30", {"entities" : qUnion([Q0, Q1]), "operationType" : NewBodyOperationType.REMOVE, "oppositeDirection" : true, "depth" : 1 * mm});
        }
        {
            var Q0;
            Q0=makeQuery(id+"F24.opExtrude","CAP_EDGE",EDGE,{"disambiguationData":[OSD([sQuery(id+"F23.wireOp",EDGE,"E159.MirrorCS")])],"isStart":false});
            var Q1;
            Q1=makeQuery(id+"F24.opExtrude","CAP_EDGE",EDGE,{"disambiguationData":[OSD([sQuery(id+"F23.wireOp",EDGE,"E158.MirrorCS")])],"isStart":false});
            var Q2;
            Q2=makeQuery(id+"F24.opExtrude","CAP_EDGE",EDGE,{"disambiguationData":[OSD([sQuery(id+"F23.wireOp",EDGE,"E159.MirrorCS")])],"isStart":true});
            var Q3;
            Q3=makeQuery(id+"F24.opExtrude","CAP_EDGE",EDGE,{"disambiguationData":[OSD([sQuery(id+"F23.wireOp",EDGE,"E158.MirrorCS")])],"isStart":true});
            var Q4;
            Q4=makeQuery(id+"F24.opExtrude","CAP_EDGE",EDGE,{"disambiguationData":[OSD([sQuery(id+"F23.wireOp",EDGE,"E157.MirrorCS")])],"isStart":true});
            var Q5;
            Q5=makeQuery(id+"F24.opExtrude","CAP_EDGE",EDGE,{"disambiguationData":[OSD([sQuery(id+"F23.wireOp",EDGE,"E155.MirrorCS")])],"isStart":true});
            var Q6;
            Q6=makeQuery(id+"F24.opExtrude","CAP_EDGE",EDGE,{"disambiguationData":[OSD([sQuery(id+"F23.wireOp",EDGE,"E155.MirrorCS")])],"isStart":false});
            var Q7;
            Q7=makeQuery(id+"F24.opExtrude","CAP_EDGE",EDGE,{"disambiguationData":[OSD([sQuery(id+"F23.wireOp",EDGE,"E157.MirrorCS")])],"isStart":false});
            var Q8;
            Q8=makeQuery(id+"F24.opExtrude","CAP_EDGE",EDGE,{"disambiguationData":[OSD([sQuery(id+"F23.wireOp",EDGE,"E152.MirrorCS")])],"isStart":false});
            var Q9;
            Q9=makeQuery(id+"F24.opExtrude","CAP_EDGE",EDGE,{"disambiguationData":[OSD([sQuery(id+"F23.wireOp",EDGE,"E152.MirrorCS")])],"isStart":true});
            var Q10;
            Q10=makeQuery(id+"F24.opExtrude","CAP_EDGE",EDGE,{"disambiguationData":[OSD([sQuery(id+"F23.wireOp",EDGE,"E154.MirrorCS")])],"isStart":true});
            var Q11;
            Q11=makeQuery(id+"F24.opExtrude","CAP_EDGE",EDGE,{"disambiguationData":[OSD([sQuery(id+"F23.wireOp",EDGE,"E154.MirrorCS")])],"isStart":false});
            var Q12;
            Q12=makeQuery(id+"F24.opExtrude","CAP_EDGE",EDGE,{"disambiguationData":[OSD([sQuery(id+"F23.wireOp",EDGE,"E150.MirrorCS")])],"isStart":false});
            var Q13;
            Q13=makeQuery(id+"F24.opExtrude","CAP_EDGE",EDGE,{"disambiguationData":[OSD([sQuery(id+"F23.wireOp",EDGE,"E150.MirrorCS")])],"isStart":true});
            var Q14;
            Q14=makeQuery(id+"F24.opExtrude","CAP_EDGE",EDGE,{"disambiguationData":[OSD([sQuery(id+"F23.wireOp",EDGE,"E149.MirrorCS")])],"isStart":true});
            var Q15;
            Q15=makeQuery(id+"F24.opExtrude","CAP_EDGE",EDGE,{"disambiguationData":[OSD([sQuery(id+"F23.wireOp",EDGE,"E149.MirrorCS")])],"isStart":false});
            var Q16;
            Q16=makeQuery(id+"F24.opExtrude","CAP_EDGE",EDGE,{"disambiguationData":[OSD([sQuery(id+"F23.wireOp",EDGE,"E148.MirrorCS")])],"isStart":true});
            var Q17;
            Q17=makeQuery(id+"F24.opExtrude","CAP_EDGE",EDGE,{"disambiguationData":[OSD([sQuery(id+"F23.wireOp",EDGE,"E148.MirrorCS")])],"isStart":false});
            var Q18;
            Q18=makeQuery(id+"F24.opExtrude","CAP_EDGE",EDGE,{"disambiguationData":[OSD([sQuery(id+"F23.wireOp",EDGE,"E146.MirrorCS")])],"isStart":false});
            var Q19;
            Q19=makeQuery(id+"F24.opExtrude","CAP_EDGE",EDGE,{"disambiguationData":[OSD([sQuery(id+"F23.wireOp",EDGE,"E146.MirrorCS")])],"isStart":true});
            var Q20;
            Q20=makeQuery(id+"F24.opExtrude","CAP_EDGE",EDGE,{"disambiguationData":[OSD([sQuery(id+"F23.wireOp",EDGE,"E137.MirrorCS")])],"isStart":true});
            var Q21;
            Q21=makeQuery(id+"F24.opExtrude","CAP_EDGE",EDGE,{"disambiguationData":[OSD([sQuery(id+"F23.wireOp",EDGE,"E137.MirrorCS")])],"isStart":false});
            var Q22;
            Q22=makeQuery(id+"F24.opExtrude","CAP_EDGE",EDGE,{"disambiguationData":[OSD([sQuery(id+"F23.wireOp",EDGE,"E139.MirrorCS")])],"isStart":false});
            var Q23;
            Q23=makeQuery(id+"F24.opExtrude","CAP_EDGE",EDGE,{"disambiguationData":[OSD([sQuery(id+"F23.wireOp",EDGE,"E139.MirrorCS")])],"isStart":true});
            var Q24;
            Q24=makeQuery(id+"F24.opExtrude","CAP_EDGE",EDGE,{"disambiguationData":[OSD([sQuery(id+"F23.wireOp",EDGE,"E140.MirrorCS")])],"isStart":true});
            var Q25;
            Q25=makeQuery(id+"F24.opExtrude","CAP_EDGE",EDGE,{"disambiguationData":[OSD([sQuery(id+"F23.wireOp",EDGE,"E140.MirrorCS")])],"isStart":false});
            var Q26;
            Q26=makeQuery(id+"F24.opExtrude","CAP_EDGE",EDGE,{"disambiguationData":[OSD([sQuery(id+"F23.wireOp",EDGE,"E142.MirrorCS")])],"isStart":false});
            var Q27;
            Q27=makeQuery(id+"F24.opExtrude","CAP_EDGE",EDGE,{"disambiguationData":[OSD([sQuery(id+"F23.wireOp",EDGE,"E142.MirrorCS")])],"isStart":true});
            var Q28;
            Q28=makeQuery(id+"F24.opExtrude","CAP_EDGE",EDGE,{"disambiguationData":[OSD([sQuery(id+"F23.wireOp",EDGE,"E143.MirrorCS")])],"isStart":true});
            var Q29;
            Q29=makeQuery(id+"F24.opExtrude","CAP_EDGE",EDGE,{"disambiguationData":[OSD([sQuery(id+"F23.wireOp",EDGE,"E143.MirrorCS")])],"isStart":false});
            var Q30;
            Q30=makeQuery(id+"F24.opExtrude","CAP_EDGE",EDGE,{"disambiguationData":[OSD([sQuery(id+"F23.wireOp",EDGE,"E145.MirrorCS")])],"isStart":true});
            var Q31;
            Q31=makeQuery(id+"F24.opExtrude","CAP_EDGE",EDGE,{"disambiguationData":[OSD([sQuery(id+"F23.wireOp",EDGE,"E145.MirrorCS")])],"isStart":false});
            var Q32;
            Q32=makeQuery(id+"F24.opExtrude","CAP_EDGE",EDGE,{"disambiguationData":[OSD([sQuery(id+"F23.wireOp",EDGE,"E122")])],"isStart":true});
            var Q33;
            Q33=makeQuery(id+"F24.opExtrude","CAP_EDGE",EDGE,{"disambiguationData":[OSD([sQuery(id+"F23.wireOp",EDGE,"E122")])],"isStart":false});
            var Q34;
            Q34=makeQuery(id+"F24.opExtrude","CAP_EDGE",EDGE,{"disambiguationData":[OSD([sQuery(id+"F23.wireOp",EDGE,"E121")])],"isStart":true});
            var Q35;
            Q35=makeQuery(id+"F24.opExtrude","CAP_EDGE",EDGE,{"disambiguationData":[OSD([sQuery(id+"F23.wireOp",EDGE,"E121")])],"isStart":false});
            var Q36;
            Q36=makeQuery(id+"F24.opExtrude","CAP_EDGE",EDGE,{"disambiguationData":[OSD([sQuery(id+"F23.wireOp",EDGE,"E127.MirrorCS")])],"isStart":true});
            var Q37;
            Q37=makeQuery(id+"F24.opExtrude","CAP_EDGE",EDGE,{"disambiguationData":[OSD([sQuery(id+"F23.wireOp",EDGE,"E127.MirrorCS")])],"isStart":false});
            var Q38;
            Q38=makeQuery(id+"F24.opExtrude","CAP_EDGE",EDGE,{"disambiguationData":[OSD([sQuery(id+"F23.wireOp",EDGE,"E126.MirrorCS")])],"isStart":true});
            var Q39;
            Q39=makeQuery(id+"F24.opExtrude","CAP_EDGE",EDGE,{"disambiguationData":[OSD([sQuery(id+"F23.wireOp",EDGE,"E126.MirrorCS")])],"isStart":false});
            var Q40;
            Q40=makeQuery(id+"F24.opExtrude","CAP_EDGE",EDGE,{"disambiguationData":[OSD([sQuery(id+"F23.wireOp",EDGE,"E131.MirrorCS")])],"isStart":true});
            var Q41;
            Q41=makeQuery(id+"F24.opExtrude","CAP_EDGE",EDGE,{"disambiguationData":[OSD([sQuery(id+"F23.wireOp",EDGE,"E131.MirrorCS")])],"isStart":false});
            var Q42;
            Q42=makeQuery(id+"F24.opExtrude","CAP_EDGE",EDGE,{"disambiguationData":[OSD([sQuery(id+"F23.wireOp",EDGE,"E130.MirrorCS")])],"isStart":true});
            var Q43;
            Q43=makeQuery(id+"F24.opExtrude","CAP_EDGE",EDGE,{"disambiguationData":[OSD([sQuery(id+"F23.wireOp",EDGE,"E130.MirrorCS")])],"isStart":false});
            var Q44;
            Q44=makeQuery(id+"F24.opExtrude","CAP_EDGE",EDGE,{"disambiguationData":[OSD([sQuery(id+"F23.wireOp",EDGE,"E136.MirrorCS")])],"isStart":true});
            var Q45;
            Q45=makeQuery(id+"F24.opExtrude","CAP_EDGE",EDGE,{"disambiguationData":[OSD([sQuery(id+"F23.wireOp",EDGE,"E136.MirrorCS")])],"isStart":false});
            var Q46;
            Q46=makeQuery(id+"F24.opExtrude","CAP_EDGE",EDGE,{"disambiguationData":[OSD([sQuery(id+"F23.wireOp",EDGE,"E134.MirrorCS")])],"isStart":true});
            var Q47;
            Q47=makeQuery(id+"F24.opExtrude","CAP_EDGE",EDGE,{"disambiguationData":[OSD([sQuery(id+"F23.wireOp",EDGE,"E134.MirrorCS")])],"isStart":false});
            fillet(context, id + "F31", {"entities" : qUnion([Q0, Q1, Q2, Q3, Q4, Q5, Q6, Q7, Q8, Q9, Q10, Q11, Q12, Q13, Q14, Q15, Q16, Q17, Q18, Q19, Q20, Q21, Q22, Q23, Q24, Q25, Q26, Q27, Q28, Q29, Q30, Q31, Q32, Q33, Q34, Q35, Q36, Q37, Q38, Q39, Q40, Q41, Q42, Q43, Q44, Q45, Q46, Q47]), "radius" : 2 * mm, "tangentPropagation" : true, "allowEdgeOverflow" : false});
        }
        {
            var Q0;
            {var subQ0=sQuery(id+"F29.wireOp",EDGE,"E164");var subQ1=sQuery(id+"F25.wireOp",EDGE,"E161");var subQ2=makeQuery(id+"F27.opExtrude","CAP_FACE",FACE,{"disambiguationData":[OSD([subQ1])],"isStart":false});Q0=makeQuery(id+"F30.boolean.opBoolean","SPLIT",FACE,{"disambiguationData":[TD([makeQuery(id+"F30.opExtrude","SWEPT_FACE",FACE,{"disambiguationData":[OSD([subQ0])]})])],"derivedFrom":subQ2});}
            var sketch = newSketch(context, id + "F32", { "sketchPlane" : qUnion([Q0])});
            skCircle(sketch, "E169.0", {"center": v(44.73, 47.66) * mm, "radius": 25.75 * mm, "construction": true});
            skLineSegment(sketch, "E170", {"start": v(18.98, 47.66) * mm, "end": v(70.48, 47.66) * mm, "construction": true});
            skLineSegment(sketch, "E171", {"start": v(44.73, 32.64) * mm, "end": v(44.73, 62.68) * mm, "construction": true});
            skLineSegment(sketch, "E172.bottom", {"start": v(22.48, 46.9) * mm, "end": v(15.48, 46.9) * mm});
            skLineSegment(sketch, "E172.top", {"start": v(22.48, 48.4) * mm, "end": v(15.48, 48.4) * mm});
            skLineSegment(sketch, "E172.left", {"start": v(22.48, 46.9) * mm, "end": v(22.48, 48.4) * mm});
            skLineSegment(sketch, "E172.right", {"start": v(15.48, 46.9) * mm, "end": v(15.48, 48.4) * mm});
            skPoint(sketch, "E172.middle", {"position": v(18.98, 47.66) * mm});
            skLineSegment(sketch, "E173.MirrorCS", {"start": v(66.98, 46.9) * mm, "end": v(66.98, 48.4) * mm});
            skLineSegment(sketch, "E174.MirrorCS", {"start": v(73.98, 46.9) * mm, "end": v(73.98, 48.4) * mm});
            skLineSegment(sketch, "E175.MirrorCS", {"start": v(66.98, 46.9) * mm, "end": v(73.98, 46.9) * mm});
            skLineSegment(sketch, "E176.MirrorCS", {"start": v(66.98, 48.4) * mm, "end": v(73.98, 48.4) * mm});
            skSolve(sketch);
        }
        {
            var Q0;
            Q0=qSketchRegion(id+"F32",true);
            extrude(context, id + "F33", {"entities" : qUnion([Q0]), "operationType" : NewBodyOperationType.REMOVE, "oppositeDirection" : true, "depth" : 5 * mm});
        }
        {
            var Q0;
            Q0=qCreatedBy(makeId("Top.planeOp"),FACE);
            var sketch = newSketch(context, id + "F34", { "sketchPlane" : qUnion([Q0])});
            skCircle(sketch, "E177", {"center": v(48, -44.82) * mm, "radius": 20.25 * mm});
            skSolve(sketch);
        }
        {
            var Q0;
            Q0=makeQuery(id+"F34.imprint","IMPRINT",FACE,{"disambiguationData":[TD([[makeQuery(id+"F34.imprint","IMPRINT",EDGE,{"derivedFrom":sQuery(id+"F34.wireOp",EDGE,"E177")}),1.0]])]});
            extrude(context, id + "F35", {"entities" : qUnion([Q0]), "depth" : 2.5 * mm});
        }
        {
            var Q0;
            Q0=makeQuery(id+"F35.opExtrude","CAP_FACE",FACE,{"disambiguationData":[OSD([sQuery(id+"F34.wireOp",EDGE,"E177")])],"isStart":false});
            var sketch = newSketch(context, id + "F36", { "sketchPlane" : qUnion([Q0])});
            skCircle(sketch, "E178", {"center": v(48, -44.82) * mm, "radius": 18 * mm});
            skLineSegment(sketch, "E179", {"start": v(30, -44.82) * mm, "end": v(66, -44.82) * mm, "construction": true});
            skLineSegment(sketch, "E180", {"start": v(48, -62.82) * mm, "end": v(48, -26.82) * mm, "construction": true});
            skLineSegment(sketch, "E181", {"start": v(31.37, -51.7) * mm, "end": v(48, -44.82) * mm, "construction": true});
            skLineSegment(sketch, "E182", {"start": v(35.27, -57.55) * mm, "end": v(48, -44.82) * mm, "construction": true});
            skLineSegment(sketch, "E183", {"start": v(30.35, -48.33) * mm, "end": v(48, -44.82) * mm, "construction": true});
            skLineSegment(sketch, "E184", {"start": v(30.02, -45.57) * mm, "end": v(31.52, -45.57) * mm});
            skLineSegment(sketch, "E185", {"start": v(31.52, -45.57) * mm, "end": v(31.52, -44.07) * mm});
            skLineSegment(sketch, "E186", {"start": v(31.52, -44.07) * mm, "end": v(30.02, -44.07) * mm});
            skPoint(sketch, "E187", {"position": v(31.52, -44.82) * mm});
            skLineSegment(sketch, "E188.MirrorCS", {"start": v(33.06, -51.82) * mm, "end": v(31.67, -52.4) * mm});
            skLineSegment(sketch, "E189.MirrorCS", {"start": v(31.1, -51) * mm, "end": v(32.49, -50.43) * mm});
            skLineSegment(sketch, "E190.MirrorCS", {"start": v(32.49, -50.43) * mm, "end": v(33.06, -51.82) * mm});
            skLineSegment(sketch, "E191.MirrorCS", {"start": v(35.82, -55.94) * mm, "end": v(36.88, -57) * mm});
            skLineSegment(sketch, "E192.MirrorCS", {"start": v(36.88, -57) * mm, "end": v(35.82, -58.07) * mm});
            skLineSegment(sketch, "E193.MirrorCS", {"start": v(34.76, -57) * mm, "end": v(35.82, -55.94) * mm});
            skLineSegment(sketch, "E194.MirrorCS", {"start": v(41.81, -61.72) * mm, "end": v(42.39, -60.33) * mm});
            skLineSegment(sketch, "E195.MirrorCS", {"start": v(41, -59.76) * mm, "end": v(40.43, -61.15) * mm});
            skLineSegment(sketch, "E196.MirrorCS", {"start": v(42.39, -60.33) * mm, "end": v(41, -59.76) * mm});
            skLineSegment(sketch, "E197.MirrorCS", {"start": v(48.75, -61.3) * mm, "end": v(48.75, -62.8) * mm});
            skLineSegment(sketch, "E198.MirrorCS", {"start": v(47.25, -62.8) * mm, "end": v(47.25, -61.3) * mm});
            skLineSegment(sketch, "E199.MirrorCS", {"start": v(47.25, -61.3) * mm, "end": v(48.75, -61.3) * mm});
            skLineSegment(sketch, "E200.MirrorCS", {"start": v(31.1, -38.63) * mm, "end": v(32.49, -39.2) * mm});
            skLineSegment(sketch, "E201.MirrorCS", {"start": v(32.49, -39.2) * mm, "end": v(33.06, -37.82) * mm});
            skLineSegment(sketch, "E202.MirrorCS", {"start": v(33.06, -37.82) * mm, "end": v(31.67, -37.24) * mm});
            skLineSegment(sketch, "E203.MirrorCS", {"start": v(34.76, -32.63) * mm, "end": v(35.82, -33.7) * mm});
            skLineSegment(sketch, "E204.MirrorCS", {"start": v(35.82, -33.7) * mm, "end": v(36.88, -32.63) * mm});
            skLineSegment(sketch, "E205.MirrorCS", {"start": v(36.88, -32.63) * mm, "end": v(35.82, -31.57) * mm});
            skLineSegment(sketch, "E206.MirrorCS", {"start": v(41, -29.88) * mm, "end": v(40.43, -28.49) * mm});
            skLineSegment(sketch, "E207.MirrorCS", {"start": v(41.81, -27.92) * mm, "end": v(42.39, -29.3) * mm});
            skLineSegment(sketch, "E208.MirrorCS", {"start": v(42.39, -29.3) * mm, "end": v(41, -29.88) * mm});
            skLineSegment(sketch, "E209.MirrorCS", {"start": v(47.25, -26.83) * mm, "end": v(47.25, -28.33) * mm});
            skLineSegment(sketch, "E210.MirrorCS", {"start": v(48.75, -28.33) * mm, "end": v(48.75, -26.83) * mm});
            skLineSegment(sketch, "E211.MirrorCS", {"start": v(47.25, -28.33) * mm, "end": v(48.75, -28.33) * mm});
            skLineSegment(sketch, "E212.MirrorCS", {"start": v(54.2, -27.92) * mm, "end": v(53.62, -29.3) * mm});
            skLineSegment(sketch, "E213.MirrorCS", {"start": v(53.62, -29.3) * mm, "end": v(55, -29.88) * mm});
            skLineSegment(sketch, "E214.MirrorCS", {"start": v(55, -29.88) * mm, "end": v(55.58, -28.49) * mm});
            skLineSegment(sketch, "E215.MirrorCS", {"start": v(59.13, -32.63) * mm, "end": v(60.19, -31.57) * mm});
            skLineSegment(sketch, "E216.MirrorCS", {"start": v(60.19, -33.7) * mm, "end": v(59.13, -32.63) * mm});
            skLineSegment(sketch, "E217.MirrorCS", {"start": v(61.25, -32.63) * mm, "end": v(60.19, -33.7) * mm});
            skLineSegment(sketch, "E218.MirrorCS", {"start": v(62.95, -37.82) * mm, "end": v(64.33, -37.24) * mm});
            skLineSegment(sketch, "E219.MirrorCS", {"start": v(63.52, -39.2) * mm, "end": v(62.95, -37.82) * mm});
            skLineSegment(sketch, "E220.MirrorCS", {"start": v(64.9, -38.63) * mm, "end": v(63.52, -39.2) * mm});
            skLineSegment(sketch, "E221.MirrorCS", {"start": v(64.49, -44.07) * mm, "end": v(65.99, -44.07) * mm});
            skLineSegment(sketch, "E222.MirrorCS", {"start": v(64.49, -45.57) * mm, "end": v(64.49, -44.07) * mm});
            skLineSegment(sketch, "E223.MirrorCS", {"start": v(65.99, -45.57) * mm, "end": v(64.49, -45.57) * mm});
            skLineSegment(sketch, "E224.MirrorCS", {"start": v(64.9, -51) * mm, "end": v(63.52, -50.43) * mm});
            skLineSegment(sketch, "E225.MirrorCS", {"start": v(63.52, -50.43) * mm, "end": v(62.95, -51.82) * mm});
            skLineSegment(sketch, "E226.MirrorCS", {"start": v(62.95, -51.82) * mm, "end": v(64.33, -52.4) * mm});
            skLineSegment(sketch, "E227.MirrorCS", {"start": v(61.25, -57) * mm, "end": v(60.19, -55.94) * mm});
            skLineSegment(sketch, "E228.MirrorCS", {"start": v(60.19, -55.94) * mm, "end": v(59.13, -57) * mm});
            skLineSegment(sketch, "E229.MirrorCS", {"start": v(59.13, -57) * mm, "end": v(60.19, -58.07) * mm});
            skLineSegment(sketch, "E230.MirrorCS", {"start": v(55, -59.76) * mm, "end": v(55.58, -61.15) * mm});
            skLineSegment(sketch, "E231.MirrorCS", {"start": v(53.62, -60.33) * mm, "end": v(55, -59.76) * mm});
            skLineSegment(sketch, "E232.MirrorCS", {"start": v(54.2, -61.72) * mm, "end": v(53.62, -60.33) * mm});
            skSolve(sketch);
        }
        {
            var Q0;
            {var subQ21=sQuery(id+"F36.wireOp",EDGE,"E184");Q0=makeQuery(id+"F36.imprint","IMPRINT",FACE,{"disambiguationData":[TD([[makeQuery(id+"F36.imprint","IMPRINT",EDGE,{"derivedFrom":subQ21}),-1.0]])]});}
            extrude(context, id + "F37", {"entities" : qUnion([Q0]), "operationType" : NewBodyOperationType.ADD, "depth" : 19.5 * mm});
        }
        {
            var Q0;
            Q0=makeQuery(id+"F37.opExtrude","CAP_FACE",FACE,{"disambiguationData":[OSD([sQuery(id+"F36.wireOp",EDGE,"E178"),sQuery(id+"F36.wireOp",EDGE,"E184"),sQuery(id+"F36.wireOp",EDGE,"E185"),sQuery(id+"F36.wireOp",EDGE,"E186"),sQuery(id+"F36.wireOp",EDGE,"E188.MirrorCS"),sQuery(id+"F36.wireOp",EDGE,"E189.MirrorCS"),sQuery(id+"F36.wireOp",EDGE,"E190.MirrorCS"),sQuery(id+"F36.wireOp",EDGE,"E191.MirrorCS"),sQuery(id+"F36.wireOp",EDGE,"E192.MirrorCS"),sQuery(id+"F36.wireOp",EDGE,"E193.MirrorCS"),sQuery(id+"F36.wireOp",EDGE,"E194.MirrorCS"),sQuery(id+"F36.wireOp",EDGE,"E195.MirrorCS"),sQuery(id+"F36.wireOp",EDGE,"E196.MirrorCS"),sQuery(id+"F36.wireOp",EDGE,"E197.MirrorCS"),sQuery(id+"F36.wireOp",EDGE,"E198.MirrorCS"),sQuery(id+"F36.wireOp",EDGE,"E199.MirrorCS"),sQuery(id+"F36.wireOp",EDGE,"E200.MirrorCS"),sQuery(id+"F36.wireOp",EDGE,"E201.MirrorCS"),sQuery(id+"F36.wireOp",EDGE,"E202.MirrorCS"),sQuery(id+"F36.wireOp",EDGE,"E203.MirrorCS"),sQuery(id+"F36.wireOp",EDGE,"E204.MirrorCS"),sQuery(id+"F36.wireOp",EDGE,"E205.MirrorCS"),sQuery(id+"F36.wireOp",EDGE,"E206.MirrorCS"),sQuery(id+"F36.wireOp",EDGE,"E207.MirrorCS"),sQuery(id+"F36.wireOp",EDGE,"E208.MirrorCS"),sQuery(id+"F36.wireOp",EDGE,"E209.MirrorCS"),sQuery(id+"F36.wireOp",EDGE,"E210.MirrorCS"),sQuery(id+"F36.wireOp",EDGE,"E211.MirrorCS"),sQuery(id+"F36.wireOp",EDGE,"E212.MirrorCS"),sQuery(id+"F36.wireOp",EDGE,"E213.MirrorCS"),sQuery(id+"F36.wireOp",EDGE,"E214.MirrorCS"),sQuery(id+"F36.wireOp",EDGE,"E215.MirrorCS"),sQuery(id+"F36.wireOp",EDGE,"E216.MirrorCS"),sQuery(id+"F36.wireOp",EDGE,"E217.MirrorCS"),sQuery(id+"F36.wireOp",EDGE,"E218.MirrorCS"),sQuery(id+"F36.wireOp",EDGE,"E219.MirrorCS"),sQuery(id+"F36.wireOp",EDGE,"E220.MirrorCS"),sQuery(id+"F36.wireOp",EDGE,"E221.MirrorCS"),sQuery(id+"F36.wireOp",EDGE,"E222.MirrorCS"),sQuery(id+"F36.wireOp",EDGE,"E223.MirrorCS"),sQuery(id+"F36.wireOp",EDGE,"E224.MirrorCS"),sQuery(id+"F36.wireOp",EDGE,"E225.MirrorCS"),sQuery(id+"F36.wireOp",EDGE,"E226.MirrorCS"),sQuery(id+"F36.wireOp",EDGE,"E227.MirrorCS"),sQuery(id+"F36.wireOp",EDGE,"E228.MirrorCS"),sQuery(id+"F36.wireOp",EDGE,"E229.MirrorCS"),sQuery(id+"F36.wireOp",EDGE,"E230.MirrorCS"),sQuery(id+"F36.wireOp",EDGE,"E231.MirrorCS"),sQuery(id+"F36.wireOp",EDGE,"E232.MirrorCS")])],"isStart":false});
            var sketch = newSketch(context, id + "F38", { "sketchPlane" : qUnion([Q0])});
            skCircle(sketch, "E233.0", {"center": v(48, -44.82) * mm, "radius": 18 * mm});
            skSolve(sketch);
        }
        {
            var Q0;
            Q0=qSketchRegion(id+"F38",true);
            extrude(context, id + "F39", {"entities" : qUnion([Q0]), "operationType" : NewBodyOperationType.ADD, "depth" : 4.5 * mm});
        }
        {
            var Q0;
            Q0=makeQuery(id+"F35.opExtrude","CAP_EDGE",EDGE,{"disambiguationData":[OSD([sQuery(id+"F34.wireOp",EDGE,"E177")])],"isStart":false});
            chamfer(context, id + "F40", {"entities" : qUnion([Q0]), "chamferType" : ChamferType.OFFSET_ANGLE, "width" : 2.5 * mm, "oppositeDirection" : true, "angle" : 42 * degree, "tangentPropagation" : true});
        }
        {
            var Q0;
            Q0=makeQuery(id+"F39.opExtrude","CAP_EDGE",EDGE,{"disambiguationData":[OSD([sQuery(id+"F38.wireOp",EDGE,"E233.0")])],"isStart":false});
            chamfer(context, id + "F41", {"entities" : qUnion([Q0]), "width" : 4.5 * mm, "tangentPropagation" : true});
        }
        {
            var Q0;
            Q0=makeQuery(id+"F39.opExtrude","CAP_FACE",FACE,{"disambiguationData":[OSD([sQuery(id+"F38.wireOp",EDGE,"E233.0")])],"isStart":false});
            var sketch = newSketch(context, id + "F42", { "sketchPlane" : qUnion([Q0])});
            skCircle(sketch, "E234.0", {"center": v(48, -44.82) * mm, "radius": 13.5 * mm});
            skCircle(sketch, "E234.1", {"center": v(48, -44.82) * mm, "radius": 18 * mm});
            skLineSegment(sketch, "E235", {"start": v(30.35, -48.33) * mm, "end": v(65.66, -41.3) * mm, "construction": true});
            skLineSegment(sketch, "E236", {"start": v(51.51, -62.47) * mm, "end": v(44.5, -27.16) * mm, "construction": true});
            skLineSegment(sketch, "E237", {"start": v(30.15, -47.1) * mm, "end": v(34.57, -46.21) * mm});
            skLineSegment(sketch, "E238.MirrorCS", {"start": v(30.63, -49.55) * mm, "end": v(35.06, -48.67) * mm});
            skLineSegment(sketch, "E239.MirrorCS", {"start": v(65.86, -42.54) * mm, "end": v(61.43, -43.42) * mm});
            skLineSegment(sketch, "E240.MirrorCS", {"start": v(65.37, -40.09) * mm, "end": v(60.94, -40.97) * mm});
            skPoint(sketch, "E241.0", {"position": v(30.02, -45.57) * mm});
            skPoint(sketch, "E241.1", {"position": v(31.1, -51) * mm});
            skLineSegment(sketch, "E242", {"start": v(31.1, -51) * mm, "end": v(48, -44.82) * mm, "construction": true});
            skLineSegment(sketch, "E243", {"start": v(30.02, -45.57) * mm, "end": v(48, -44.82) * mm, "construction": true});
            skSolve(sketch);
        }
        {
            var Q0;
            {var subQ0=sQuery(id+"F42.wireOp",EDGE,"E237");Q0=makeQuery(id+"F42.imprint","IMPRINT",FACE,{"disambiguationData":[TD([[makeQuery(id+"F42.imprint","IMPRINT",EDGE,{"derivedFrom":subQ0}),-1.0]])]});}
            var Q1;
            {var subQ0=sQuery(id+"F42.wireOp",EDGE,"E239.MirrorCS");Q1=makeQuery(id+"F42.imprint","IMPRINT",FACE,{"disambiguationData":[TD([[makeQuery(id+"F42.imprint","IMPRINT",EDGE,{"derivedFrom":subQ0}),-1.0]])]});}
            var Q2;
            {var subQ2=sQuery(id+"F36.wireOp",EDGE,"E188.MirrorCS");var subQ3=sQuery(id+"F38.wireOp",EDGE,"E233.0");Q2=makeQuery(id+"F39.boolean.opBoolean","SPLIT",FACE,{"disambiguationData":[TD([makeQuery(id+"F37.opExtrude","SWEPT_FACE",FACE,{"disambiguationData":[OSD([subQ2])]})])],"derivedFrom":makeQuery(id+"F39.opExtrude","CAP_FACE",FACE,{"disambiguationData":[OSD([subQ3])],"isStart":true})});}
            extrude(context, id + "F43", {"entities" : qUnion([Q0, Q1]), "operationType" : NewBodyOperationType.REMOVE, "endBound" : BoundingType.UP_TO_SURFACE, "oppositeDirection" : true, "endBoundEntityFace" : qUnion([Q2]), "depth" : 4.5 * mm});
        }
    });
